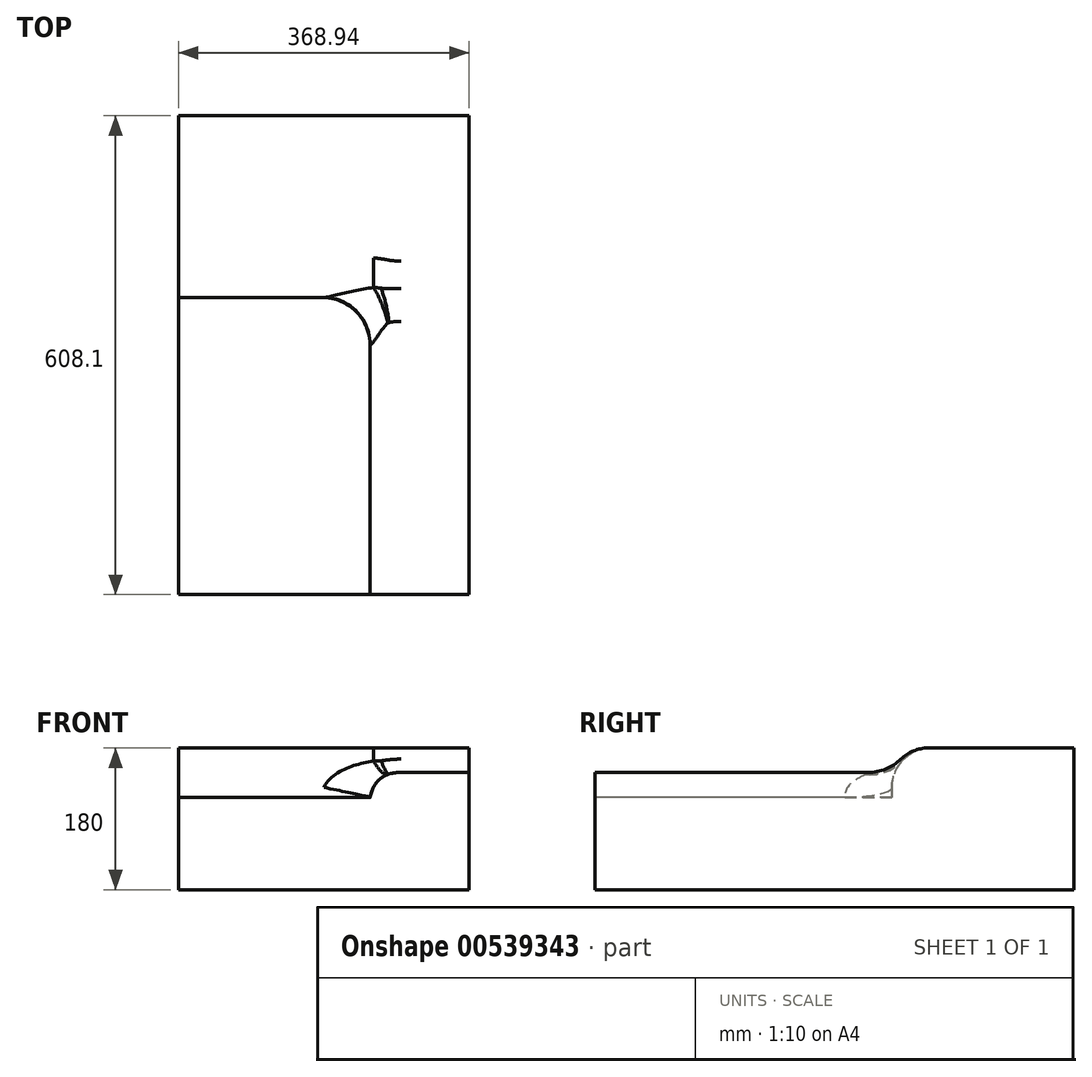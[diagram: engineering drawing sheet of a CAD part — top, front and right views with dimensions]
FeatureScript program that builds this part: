
annotation { "Feature Type Name" : "Feature", "Feature Type Description" : "" }
export const myFeature = defineFeature(function(context is Context, id is Id, definition is map)
    precondition{}
    {
        {
            var Q0;
            Q0=qCreatedBy(makeId("Top.planeOp"),FACE);
            var sketch = newSketch(context, id + "F0", { "sketchPlane" : qUnion([Q0])});
            skLineSegment(sketch, "E0.bottom", {"start": v(-308.1, -168.94) * mm, "end": v(300, -168.94) * mm});
            skLineSegment(sketch, "E0.top", {"start": v(-308.1, 200) * mm, "end": v(300, 200) * mm});
            skLineSegment(sketch, "E0.left", {"start": v(-308.1, -168.94) * mm, "end": v(-308.1, 200) * mm});
            skLineSegment(sketch, "E0.right", {"start": v(300, -168.94) * mm, "end": v(300, 200) * mm});
            skSolve(sketch);
        }
        {
            var Q0;
            Q0 = qSketchRegion(id + "F0", true);
            extrude(context, id + "F1", {"entities" : qUnion([Q0]), "flatOperationType" : FlatOperationType.REMOVE, "depth" : 117 * mm, "offsetDistance" : 25 * mm, "domain" : OperationDomain.MODEL});
        }
        {
            var Q0;
            Q0=makeQuery(id+"F1.opExtrude","CAP_FACE",FACE,{"disambiguationData":[OSD([sQuery(id+"F0.wireOp",EDGE,"E0.bottom"),sQuery(id+"F0.wireOp",EDGE,"E0.top"),sQuery(id+"F0.wireOp",EDGE,"E0.left"),sQuery(id+"F0.wireOp",EDGE,"E0.right")])],"isStart":false});
            var sketch = newSketch(context, id + "F2", { "sketchPlane" : qUnion([Q0])});
            skLineSegment(sketch, "E1.bottom", {"start": v(-308.1, 200) * mm, "end": v(-77.25, 200) * mm});
            skLineSegment(sketch, "E1.top", {"start": v(-308.1, -168.94) * mm, "end": v(-77.25, -168.94) * mm});
            skLineSegment(sketch, "E1.left", {"start": v(-308.1, 200) * mm, "end": v(-308.1, -168.94) * mm});
            skLineSegment(sketch, "E1.right", {"start": v(-77.25, 200) * mm, "end": v(-77.25, -168.94) * mm});
            skLineSegment(sketch, "E2.bottom", {"start": v(-77.25, 74.28) * mm, "end": v(300, 74.28) * mm});
            skLineSegment(sketch, "E2.top", {"start": v(-77.25, 200) * mm, "end": v(300, 200) * mm});
            skLineSegment(sketch, "E2.left", {"start": v(-77.25, 74.28) * mm, "end": v(-77.25, 200) * mm});
            skLineSegment(sketch, "E2.right", {"start": v(300, 74.28) * mm, "end": v(300, 200) * mm});
            skSolve(sketch);
        }
        {
            var Q0;
            Q0=makeQuery(id+"F2.imprint","IMPRINT",FACE,{"disambiguationData":[TD([[makeQuery(id+"F2.imprint","IMPRINT",EDGE,{"derivedFrom":sQuery(id+"F2.wireOp",EDGE,"E2.bottom")}),1.0]])]});
            extrude(context, id + "F3", {"entities" : qUnion([Q0]), "operationType" : NewBodyOperationType.ADD, "flatOperationType" : FlatOperationType.REMOVE, "depth" : 32 * mm, "offsetDistance" : 25 * mm, "domain" : OperationDomain.MODEL});
        }
        {
            var Q0;
            Q0=makeQuery(id+"F2.imprint","IMPRINT",FACE,{"disambiguationData":[TD([[makeQuery(id+"F2.imprint","IMPRINT",EDGE,{"derivedFrom":sQuery(id+"F2.wireOp",EDGE,"E1.bottom")}),-1.0]])]});
            extrude(context, id + "F4", {"entities" : qUnion([Q0]), "operationType" : NewBodyOperationType.ADD, "depth" : 63 * mm, "offsetDistance" : 25 * mm});
        }
        {
            var Q0;
            Q0=makeQuery(id+"F3.opExtrude","CAP_EDGE",EDGE,{"disambiguationData":[OSD([sQuery(id+"F2.wireOp",EDGE,"E2.bottom")])],"isStart":false});
            fillet(context, id + "F5", {"entities" : qUnion([Q0]), "radius" : 40 * mm, "rho" : 0.5, "defaultsChanged" : true, "crossSection" : FilletCrossSection.CONIC, "allowEdgeOverflow" : false, "vertexSettings" : []});
        }
        {
            var Q0;
            Q0=makeQuery(id+"F4.opExtrude","CAP_EDGE",EDGE,{"disambiguationData":[OSD([sQuery(id+"F2.wireOp",EDGE,"E1.right"),sQuery(id+"F2.wireOp",EDGE,"E2.left")])],"isStart":false});
            fillet(context, id + "F6", {"entities" : qUnion([Q0]), "radius" : 50 * mm, "tangentPropagation" : true, "allowEdgeOverflow" : false});
        }
        {
            var Q0;
            {var subQ0=sQuery(id+"F2.wireOp",EDGE,"E2.left");Q0=makeQuery(id+"F6.opFillet","BLEND_EDGE",EDGE,{"blendedFrom":[makeQuery(id+"F4.opExtrude","CAP_EDGE",EDGE,{"disambiguationData":[OSD([sQuery(id+"F2.wireOp",EDGE,"E1.right"),subQ0])],"isStart":false}),makeQuery(id+"F3.opExtrude","CAP_FACE",FACE,{"disambiguationData":[OSD([sQuery(id+"F2.wireOp",EDGE,"E2.bottom"),sQuery(id+"F2.wireOp",EDGE,"E2.top"),subQ0,sQuery(id+"F2.wireOp",EDGE,"E2.right")])],"isStart":false})],"blendedInto":[makeQuery(id+"F3.opExtrude","CAP_FACE",FACE,{"disambiguationData":[OSD([sQuery(id+"F2.wireOp",EDGE,"E2.bottom"),sQuery(id+"F2.wireOp",EDGE,"E2.top"),subQ0,sQuery(id+"F2.wireOp",EDGE,"E2.right")])],"isStart":false})]});}
            fillet(context, id + "F7", {"entities" : qUnion([Q0]), "radius" : 60 * mm, "tangentPropagation" : true, "allowEdgeOverflow" : false});
        }
        {
            var Q0;
            Q0=makeQuery(id+"F1.opExtrude","SWEPT_BODY",BODY,{"disambiguationData":[OSD([sQuery(id+"F0.wireOp",EDGE,"E0.bottom"),sQuery(id+"F0.wireOp",EDGE,"E0.top"),sQuery(id+"F0.wireOp",EDGE,"E0.left"),sQuery(id+"F0.wireOp",EDGE,"E0.right")])]});
            var Q1;
            Q1=makeQuery(id+"F3.boolean.opBoolean","MERGE",EDGE,{"derivedFrom":[makeQuery(id+"F1.opExtrude","SWEPT_EDGE",EDGE,{"disambiguationData":[OSD([sQuery(id+"F0.wireOp",EDGE,"E0.top"),sQuery(id+"F0.wireOp",EDGE,"E0.right")])]}),makeQuery(id+"F3.opExtrude","SWEPT_EDGE",EDGE,{"disambiguationData":[OSD([sQuery(id+"F2.wireOp",EDGE,"E2.top"),sQuery(id+"F2.wireOp",EDGE,"E2.right")])]})]});
            transform(context, id + "F8", {"entities" : qUnion([Q0]), "transformType" : TransformType.ROTATION, "transformAxis" : qUnion([Q1]), "angle" : 90 * degree, "makeCopy" : false});
        }
    });
